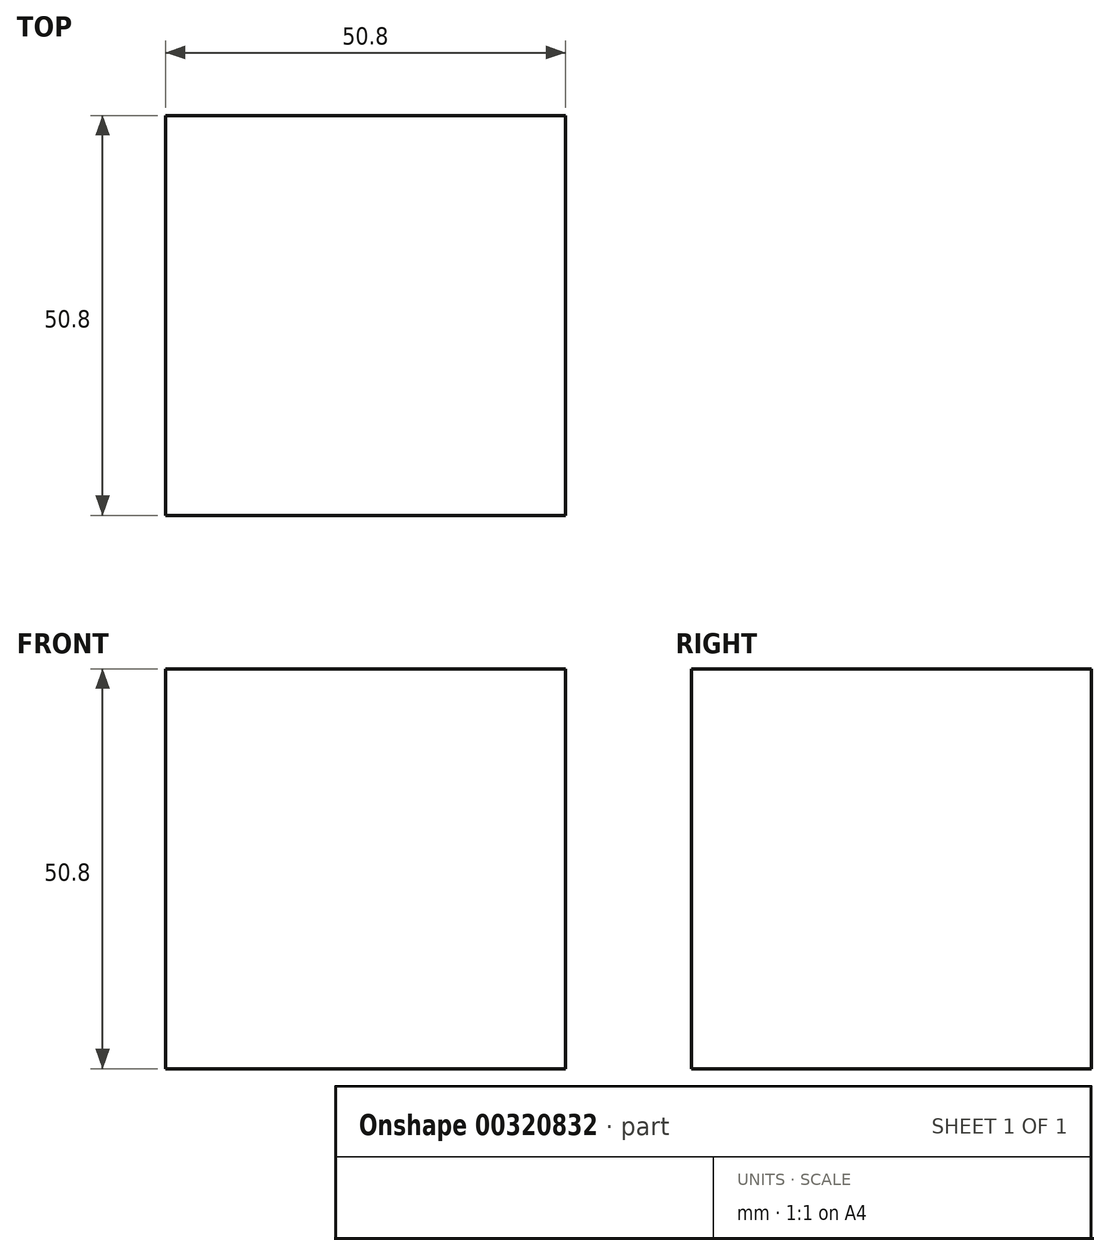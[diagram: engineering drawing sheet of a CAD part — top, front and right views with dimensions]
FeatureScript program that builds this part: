
annotation { "Feature Type Name" : "Feature", "Feature Type Description" : "" }
export const myFeature = defineFeature(function(context is Context, id is Id, definition is map)
    precondition{}
    {
        {
            var Q0;
            Q0=qCreatedBy(makeId("Front.planeOp"),FACE);
            var sketch = newSketch(context, id + "F0", { "sketchPlane" : qUnion([Q0])});
            skLineSegment(sketch, "E0.bottom", {"start": v(25.4, -25.4) * mm, "end": v(-25.4, -25.4) * mm});
            skLineSegment(sketch, "E0.top", {"start": v(25.4, 25.4) * mm, "end": v(-25.4, 25.4) * mm});
            skLineSegment(sketch, "E0.left", {"start": v(25.4, -25.4) * mm, "end": v(25.4, 25.4) * mm});
            skLineSegment(sketch, "E0.right", {"start": v(-25.4, -25.4) * mm, "end": v(-25.4, 25.4) * mm});
            skPoint(sketch, "E0.middle", {"position": v(0, 0) * mm});
            skSolve(sketch);
        }
        {
            var Q0;
            Q0 = qSketchRegion(id + "F0", true);
            extrude(context, id + "F1", {"entities" : qUnion([Q0]), "oppositeDirection" : true, "depth" : 50.8 * mm});
        }
    });
